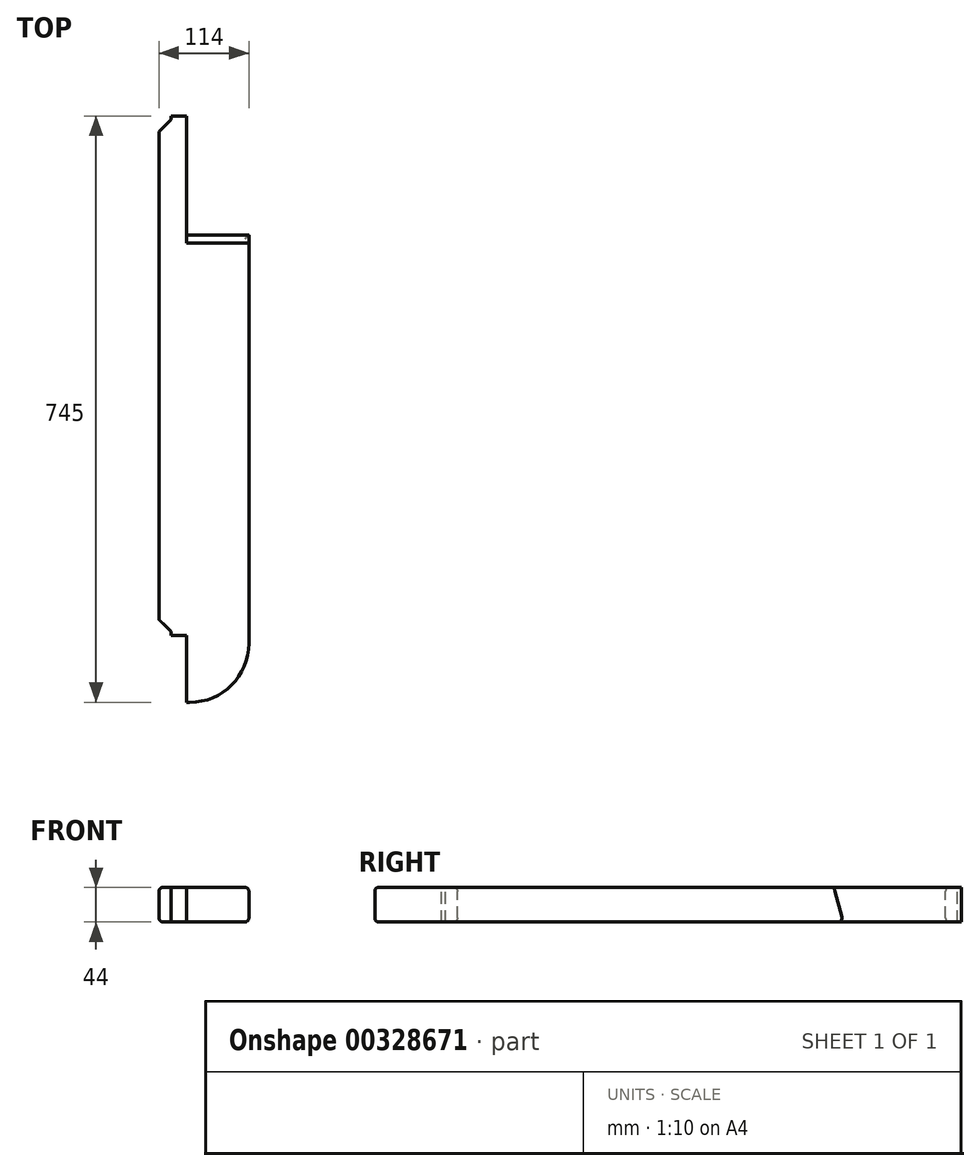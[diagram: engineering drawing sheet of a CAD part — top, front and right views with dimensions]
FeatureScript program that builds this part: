
annotation { "Feature Type Name" : "Feature", "Feature Type Description" : "" }
export const myFeature = defineFeature(function(context is Context, id is Id, definition is map)
    precondition{}
    {
        {
            var Q0;
            Q0=qCreatedBy(makeId("Top.planeOp"),FACE);
            var sketch = newSketch(context, id + "F0", { "sketchPlane" : qUnion([Q0])});
            skLineSegment(sketch, "E0.bottom", {"start": v(35, 0) * mm, "end": v(39, 0) * mm});
            skLineSegment(sketch, "E0.top", {"start": v(15, 745) * mm, "end": v(35, 745) * mm});
            skLineSegment(sketch, "E0.left", {"start": v(0, 105) * mm, "end": v(0, 725) * mm});
            skLineSegment(sketch, "E0.right", {"start": v(114, 75) * mm, "end": v(114, 595) * mm});
            skLineSegment(sketch, "E1", {"start": v(35, 0) * mm, "end": v(35, 85) * mm});
            skLineSegment(sketch, "E2", {"start": v(35, 85) * mm, "end": v(15, 85) * mm});
            skLineSegment(sketch, "E3", {"start": v(0, 0) * mm, "end": v(35, 0) * mm, "construction": true});
            skLineSegment(sketch, "E4", {"start": v(0, 0) * mm, "end": v(0, 85) * mm, "construction": true});
            skPoint(sketch, "E5.visualSharp", {"position": v(114, 0) * mm});
            skArc(sketch, "E5.filletArc", {"start": v(39, 0) * mm, "mid": v(92.03, 21.97) * mm, "end": v(114, 75) * mm});
            skLineSegment(sketch, "E6", {"start": v(0, 105) * mm, "end": v(15, 90) * mm});
            skLineSegment(sketch, "E7", {"start": v(15, 90) * mm, "end": v(15, 85) * mm});
            skLineSegment(sketch, "E8", {"start": v(114, 595) * mm, "end": v(35, 595) * mm});
            skLineSegment(sketch, "E9", {"start": v(35, 595) * mm, "end": v(35, 745) * mm});
            skLineSegment(sketch, "E10", {"start": v(0, 725) * mm, "end": v(15, 740) * mm});
            skLineSegment(sketch, "E11", {"start": v(15, 740) * mm, "end": v(15, 745) * mm});
            skPoint(sketch, "E12.orphan", {"position": v(0, 745) * mm});
            skSolve(sketch);
        }
        {
            var Q0;
            Q0=makeQuery(id+"F0.imprint","IMPRINT",FACE,{"disambiguationData":[TD([[makeQuery(id+"F0.imprint","IMPRINT",EDGE,{"derivedFrom":sQuery(id+"F0.wireOp",EDGE,"E0.bottom")}),1.0]])]});
            extrude(context, id + "F1", {"entities" : qUnion([Q0]), "oppositeDirection" : true, "depth" : 44 * mm});
        }
        {
            var Q0;
            Q0=makeQuery(id+"F1.opExtrude","SWEPT_FACE",FACE,{"disambiguationData":[OSD([sQuery(id+"F0.wireOp",EDGE,"E0.right")])]});
            var sketch = newSketch(context, id + "F2", { "sketchPlane" : qUnion([Q0])});
            skLineSegment(sketch, "E13", {"start": v(595, -44) * mm, "end": v(595, 0) * mm});
            skLineSegment(sketch, "E14", {"start": v(595, -44) * mm, "end": v(583.21, 0) * mm});
            skLineSegment(sketch, "E15", {"start": v(583.21, 0) * mm, "end": v(595, 0) * mm});
            skSolve(sketch);
        }
        {
            var Q0;
            Q0=qSketchRegion(id+"F2",true);
            extrude(context, id + "F3", {"entities" : qUnion([Q0]), "operationType" : NewBodyOperationType.REMOVE, "oppositeDirection" : true, "depth" : 79 * mm});
        }
        {
            var Q0;
            Q0=makeQuery(id+"F1.opExtrude","CAP_EDGE",EDGE,{"disambiguationData":[OSD([sQuery(id+"F0.wireOp",EDGE,"E0.right")])],"isStart":false});
            var Q1;
            Q1=makeQuery(id+"F1.opExtrude","CAP_EDGE",EDGE,{"disambiguationData":[OSD([sQuery(id+"F0.wireOp",EDGE,"E0.right")])],"isStart":true});
            var Q2;
            Q2=makeQuery(id+"F3.boolean.opBoolean","MERGE",EDGE,{"derivedFrom":[makeQuery(id+"F1.opExtrude","CAP_EDGE",EDGE,{"disambiguationData":[OSD([sQuery(id+"F0.wireOp",EDGE,"E8")])],"isStart":false}),makeQuery(id+"F3.opExtrude","SWEPT_EDGE",EDGE,{"disambiguationData":[OSD([sQuery(id+"F0.wireOp",EDGE,"E0.right"),sQuery(id+"F2.wireOp",EDGE,"E13"),sQuery(id+"F2.wireOp",EDGE,"E14")])]})]});
            var Q3;
            Q3=makeQuery(id+"F1.opExtrude","CAP_EDGE",EDGE,{"disambiguationData":[OSD([sQuery(id+"F0.wireOp",EDGE,"E0.left")])],"isStart":false});
            var Q4;
            Q4=makeQuery(id+"F1.opExtrude","CAP_EDGE",EDGE,{"disambiguationData":[OSD([sQuery(id+"F0.wireOp",EDGE,"E0.left")])],"isStart":true});
            fillet(context, id + "F4", {"entities" : qUnion([Q0, Q1, Q2, Q3, Q4]), "radius" : 5 * mm, "tangentPropagation" : true, "allowEdgeOverflow" : false});
        }
    });
